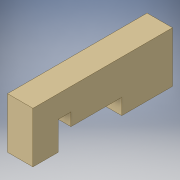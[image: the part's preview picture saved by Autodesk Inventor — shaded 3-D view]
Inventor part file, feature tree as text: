
AUTODESK INVENTOR PART (.ipt)
format: ipt  version: 2016 (Build 200138000, 138)  size: 105,472 bytes
history: native  units: in
note: dims shown in document units (in); Inventor stores cm internally (conversion verified against a paired STEP export)
features: extrude x2, sketch x2
ambient origin geometry x8: Origin, YZ Plane, XZ Plane, XY Plane, X Axis, Y Axis, Z Axis, Center Point
bodies: Solid1 (feature_tree)
feature tree (4):
  extrude  "Extrusion1"  Depth=4.0in
  extrude  "Extrusion2"  Depth=1.0in
  sketch  "Sketch1"  dims[d0=2.0in d1=4.0in]
  sketch  "Sketch2"  dims[d2=11.0in d3=0.0in d4=1.0in d5=2.25in d6=2.0in d7=4.0in d8=1.25in d9=11.0in d10=0.0in]
